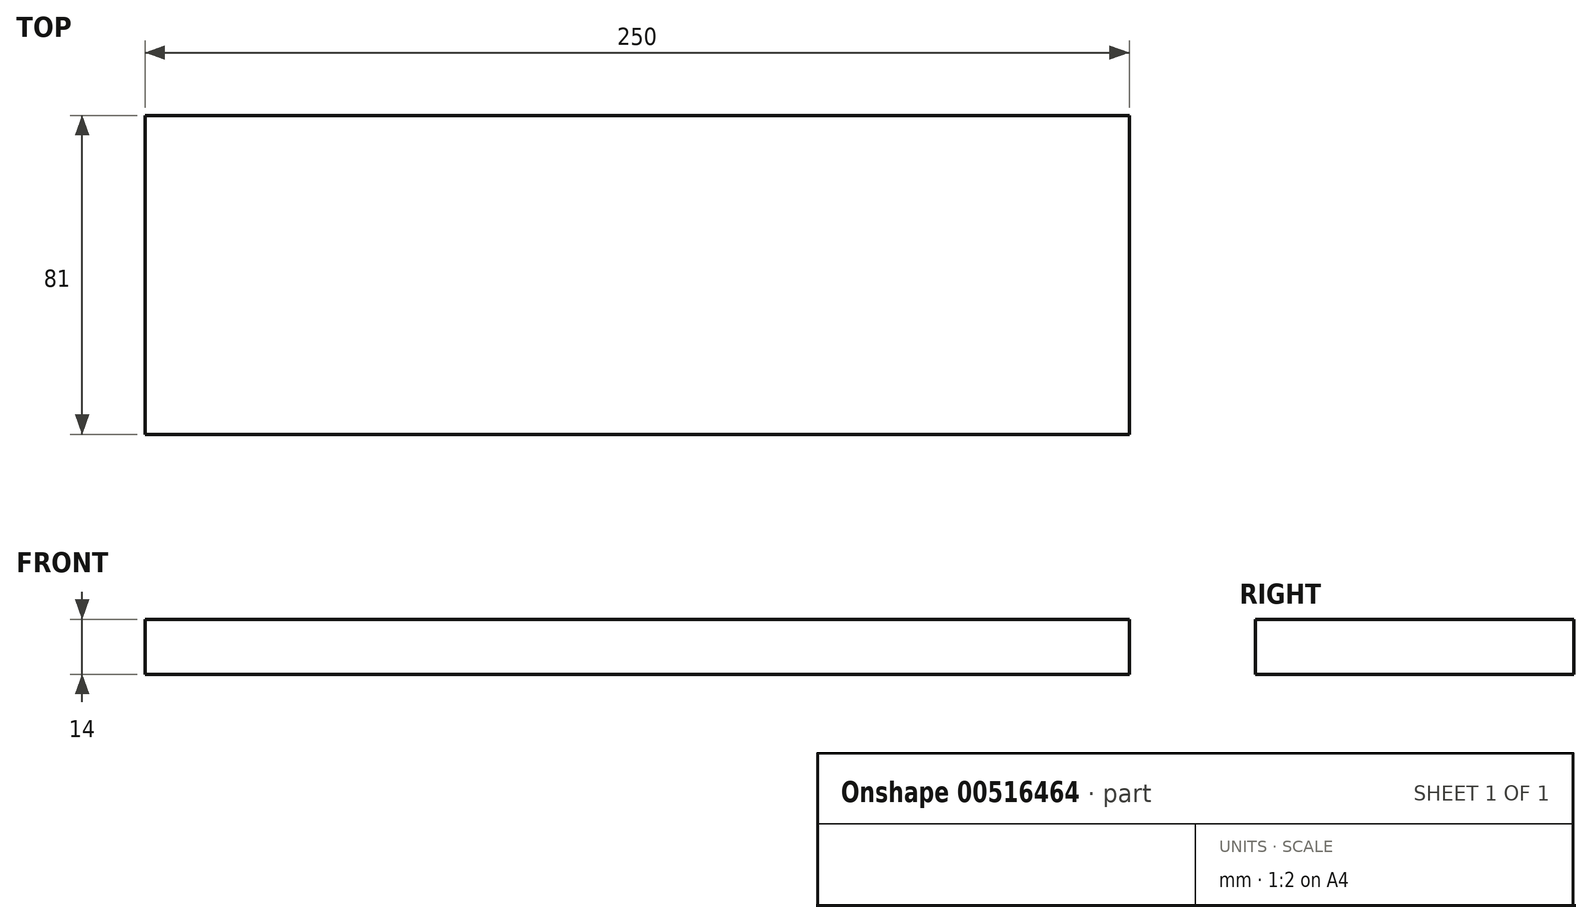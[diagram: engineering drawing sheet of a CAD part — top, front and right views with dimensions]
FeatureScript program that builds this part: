
annotation { "Feature Type Name" : "Feature", "Feature Type Description" : "" }
export const myFeature = defineFeature(function(context is Context, id is Id, definition is map)
    precondition{}
    {
        {
            var Q0;
            Q0=qCreatedBy(makeId("Top.planeOp"),FACE);
            var sketch = newSketch(context, id + "F0", { "sketchPlane" : qUnion([Q0])});
            skLineSegment(sketch, "E0.bottom", {"start": v(-54.53, -60.28) * mm, "end": v(133.47, -60.28) * mm});
            skLineSegment(sketch, "E0.top", {"start": v(-54.53, 21.72) * mm, "end": v(133.47, 21.72) * mm});
            skLineSegment(sketch, "E0.left", {"start": v(-54.53, -60.28) * mm, "end": v(-54.53, 21.72) * mm});
            skLineSegment(sketch, "E0.right", {"start": v(133.47, -60.28) * mm, "end": v(133.47, 21.72) * mm});
            skSolve(sketch);
        }
        {
            var Q0;
            Q0 = qSketchRegion(id + "F0", true);
            extrude(context, id + "F1", {"entities" : qUnion([Q0]), "depth" : 14 * mm, "offsetDistance" : 25 * mm});
        }
        {
            var Q0;
            Q0=makeQuery(id+"F1.opExtrude","SWEPT_FACE",FACE,{"disambiguationData":[OSD([sQuery(id+"F0.wireOp",EDGE,"E0.bottom")])]});
            var sketch = newSketch(context, id + "F2", { "sketchPlane" : qUnion([Q0])});
            skSolve(sketch);
        }
        {
            var Q0;
            {var subQ0=sQuery(id+"F0.wireOp",EDGE,"E0.bottom");Q0=makeQuery(id+"F2.imprint","IMPRINT",FACE,{"disambiguationData":[TD([[makeQuery(id+"F2.imprint","IMPRINT",EDGE,{"derivedFrom":makeQuery(id+"F1.opExtrude","CAP_EDGE",EDGE,{"disambiguationData":[OSD([subQ0])],"isStart":true})}),1.0]])]});}
            extrude(context, id + "F3", {"entities" : qUnion([Q0]), "operationType" : NewBodyOperationType.REMOVE, "oppositeDirection" : true, "depth" : 1 * mm, "offsetDistance" : 25 * mm});
        }
        {
            var Q0;
            Q0=makeQuery(id+"F1.opExtrude","SWEPT_FACE",FACE,{"disambiguationData":[OSD([sQuery(id+"F0.wireOp",EDGE,"E0.right")])]});
            extrude(context, id + "F4", {"entities" : qUnion([Q0]), "operationType" : NewBodyOperationType.ADD, "depth" : 62 * mm, "offsetDistance" : 25 * mm});
        }
    });
